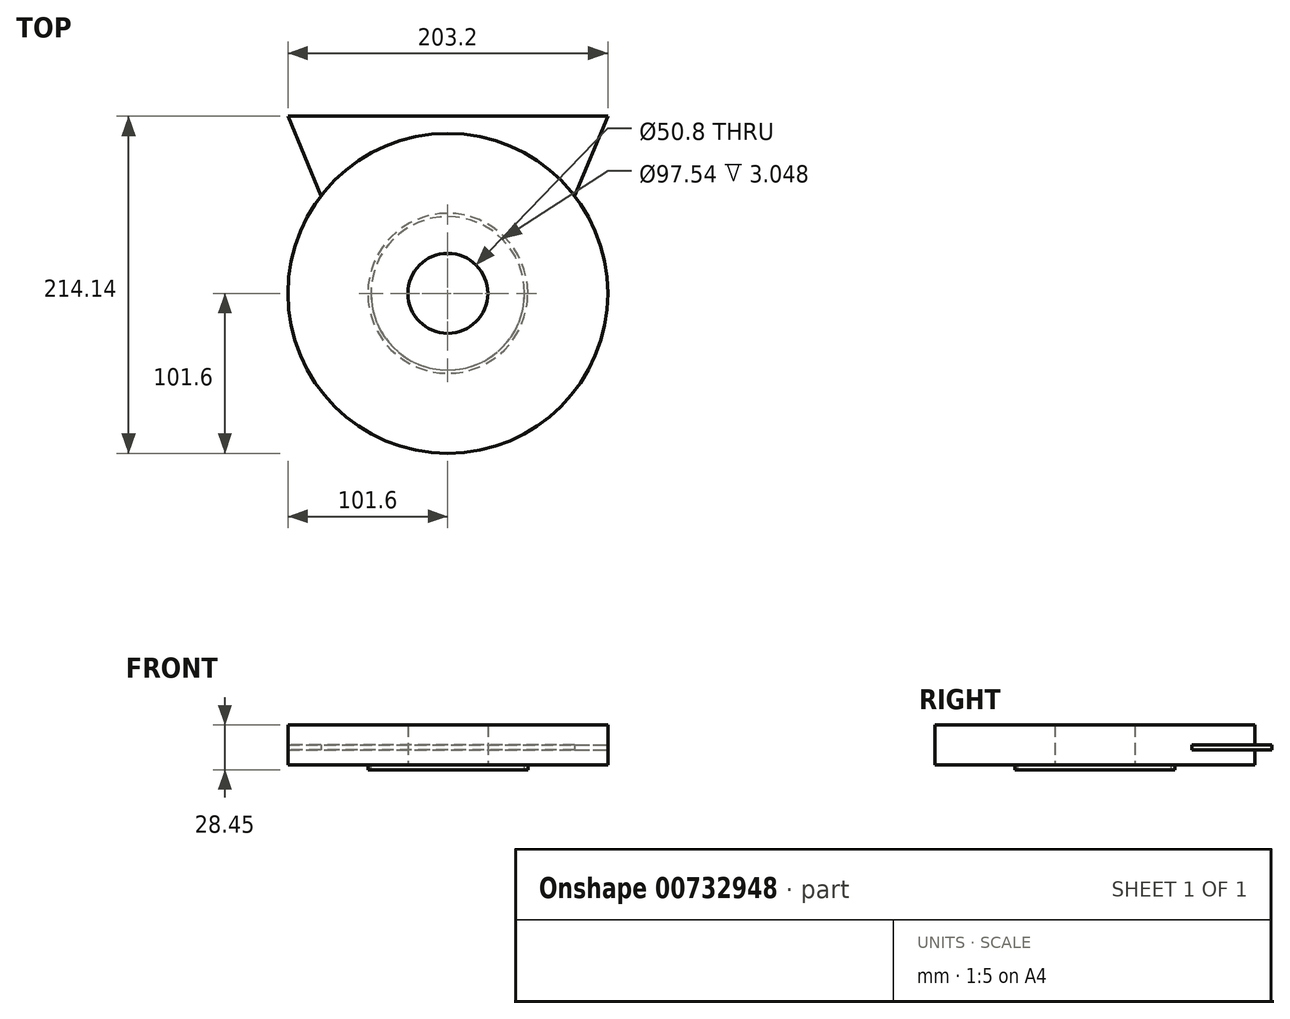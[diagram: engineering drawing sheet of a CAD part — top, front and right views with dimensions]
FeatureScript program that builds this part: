
annotation { "Feature Type Name" : "Feature", "Feature Type Description" : "" }
export const myFeature = defineFeature(function(context is Context, id is Id, definition is map)
    precondition{}
    {
        {
            var Q0;
            Q0=qCreatedBy(makeId("Top.planeOp"),FACE);
            var sketch = newSketch(context, id + "F0", { "sketchPlane" : qUnion([Q0])});
            skCircle(sketch, "E0", {"center": v(0, 0) * mm, "radius": 101.6 * mm});
            skCircle(sketch, "E1", {"center": v(0, 0) * mm, "radius": 25.4 * mm});
            skSolve(sketch);
        }
        {
            var Q0;
            Q0 = qSketchRegion(id + "F0", true);
            extrude(context, id + "F1", {"entities" : qUnion([Q0]), "endBound" : BoundingType.SYMMETRIC, "depth" : 25.4 * mm, "offsetDistance" : 25.4 * mm});
        }
        {
            var Q0;
            Q0=qCreatedBy(makeId("Top.planeOp"),FACE);
            var sketch = newSketch(context, id + "F2", { "sketchPlane" : qUnion([Q0])});
            skCircle(sketch, "E2", {"center": v(0, 0) * mm, "radius": 25.4 * mm});
            skArc(sketch, "E3", {"start": v(-46.93, -19.44) * mm, "mid": v(0, -50.8) * mm, "end": v(46.93, -19.44) * mm});
            skLineSegment(sketch, "E4", {"start": v(0, 190.85) * mm, "end": v(0, -108.62) * mm, "construction": true});
            skLineSegment(sketch, "E5", {"start": v(46.93, -19.44) * mm, "end": v(101.6, 112.54) * mm});
            skLineSegment(sketch, "E6", {"start": v(-46.93, -19.44) * mm, "end": v(-101.6, 112.54) * mm});
            skLineSegment(sketch, "E7", {"start": v(-46.93, -19.44) * mm, "end": v(46.93, -19.44) * mm, "construction": true});
            skPoint(sketch, "E8", {"position": v(0, -19.44) * mm});
            skLineSegment(sketch, "E9", {"start": v(-101.6, 112.54) * mm, "end": v(101.6, 112.54) * mm});
            skSolve(sketch);
        }
        {
            var Q0;
            Q0 = qSketchRegion(id + "F2", true);
            extrude(context, id + "F3", {"entities" : qUnion([Q0]), "oppositeDirection" : true, "depth" : 3.05 * mm, "offsetDistance" : 25.4 * mm});
        }
        {
            var Q0;
            Q0=makeQuery(id+"F3.opExtrude","CAP_FACE",FACE,{"disambiguationData":[OSD([sQuery(id+"F2.wireOp",EDGE,"E2"),sQuery(id+"F2.wireOp",EDGE,"E3"),sQuery(id+"F2.wireOp",EDGE,"E5"),sQuery(id+"F2.wireOp",EDGE,"E6"),sQuery(id+"F2.wireOp",EDGE,"E9")])],"isStart":false});
            var sketch = newSketch(context, id + "F4", { "sketchPlane" : qUnion([Q0])});
            skCircle(sketch, "E10", {"center": v(0, 0) * mm, "radius": 50.8 * mm});
            skCircle(sketch, "E11.0", {"center": v(0, 0) * mm, "radius": 48.77 * mm});
            skSolve(sketch);
        }
        {
            var Q0;
            Q0 = qSketchRegion(id + "F4", true);
            extrude(context, id + "F5", {"entities" : qUnion([Q0]), "operationType" : NewBodyOperationType.ADD, "depth" : 12.7 * mm, "offsetDistance" : 25.4 * mm});
        }
    });
